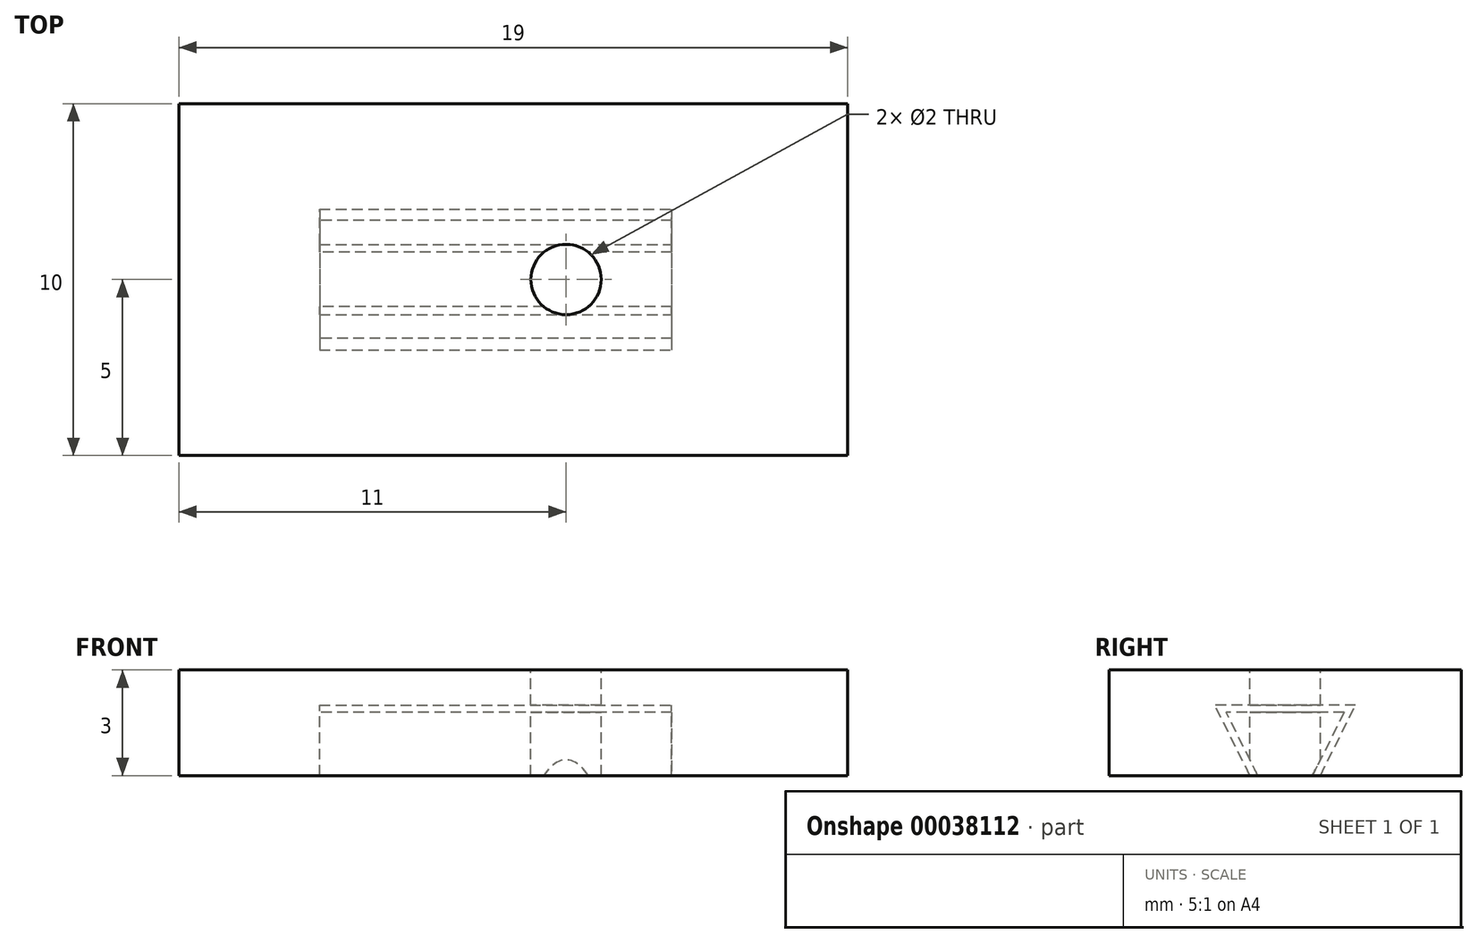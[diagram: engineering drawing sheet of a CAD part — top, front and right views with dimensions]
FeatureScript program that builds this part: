
annotation { "Feature Type Name" : "Feature", "Feature Type Description" : "" }
export const myFeature = defineFeature(function(context is Context, id is Id, definition is map)
    precondition{}
    {
        {
            var Q0;
            Q0=qCreatedBy(makeId("Top.planeOp"),FACE);
            var sketch = newSketch(context, id + "F0", { "sketchPlane" : qUnion([Q0])});
            skLineSegment(sketch, "E0.bottom", {"start": v(0, -5) * mm, "end": v(-14, -5) * mm});
            skLineSegment(sketch, "E0.top", {"start": v(0, 5) * mm, "end": v(-14, 5) * mm});
            skLineSegment(sketch, "E0.left", {"start": v(0, -5) * mm, "end": v(0, 5) * mm});
            skLineSegment(sketch, "E0.right", {"start": v(-14, -5) * mm, "end": v(-14, 5) * mm});
            skPoint(sketch, "E1", {"position": v(0, 0) * mm});
            skSolve(sketch);
        }
        {
            assignVariable(context, id + "F1", {"name" : "holed", "anyValue" : 2});
        }
        {
            var Q0;
            Q0 = qSketchRegion(id + "F0", true);
            extrude(context, id + "F2", {"entities" : qUnion([Q0]), "depth" : 3 * mm});
        }
        {
            var Q0;
            Q0=makeQuery(id+"F2.opExtrude","SWEPT_FACE",FACE,{"disambiguationData":[OSD([sQuery(id+"F0.wireOp",EDGE,"E0.left")])]});
            var sketch = newSketch(context, id + "F3", { "sketchPlane" : qUnion([Q0])});
            skLineSegment(sketch, "E2", {"start": v(0, 0) * mm, "end": v(-1, 0) * mm});
            skLineSegment(sketch, "E3", {"start": v(-1, 0) * mm, "end": v(-2, 2) * mm});
            skLineSegment(sketch, "E4", {"start": v(-2, 2) * mm, "end": v(0, 2) * mm});
            skLineSegment(sketch, "E5.MirrorCS", {"start": v(2, 2) * mm, "end": v(0, 2) * mm});
            skLineSegment(sketch, "E6.MirrorCS", {"start": v(1, 0) * mm, "end": v(2, 2) * mm});
            skLineSegment(sketch, "E7.MirrorCS", {"start": v(0, 0) * mm, "end": v(1, 0) * mm});
            skSolve(sketch);
        }
        {
            var Q0;
            Q0 = qSketchRegion(id + "F3", true);
            extrude(context, id + "F4", {"entities" : qUnion([Q0]), "operationType" : NewBodyOperationType.REMOVE, "oppositeDirection" : true, "depth" : 10 * mm});
        }
        {
            var Q0;
            Q0=makeQuery(id+"F4.boolean.opBoolean","COPY",FACE,{"derivedFrom":makeQuery(id+"F4.opExtrude","CAP_FACE",FACE,{"disambiguationData":[OSD([sQuery(id+"F3.wireOp",EDGE,"E2"),sQuery(id+"F3.wireOp",EDGE,"E3"),sQuery(id+"F3.wireOp",EDGE,"E4"),sQuery(id+"F3.wireOp",EDGE,"E5.MirrorCS"),sQuery(id+"F3.wireOp",EDGE,"E6.MirrorCS"),sQuery(id+"F3.wireOp",EDGE,"E7.MirrorCS")])],"isStart":false})});
            var sketch = newSketch(context, id + "F5", { "sketchPlane" : qUnion([Q0])});
            skLineSegment(sketch, "E8.0", {"start": v(-0.82, 0.09) * mm, "end": v(-1.68, 1.8) * mm});
            skLineSegment(sketch, "E8.1", {"start": v(1.68, 1.8) * mm, "end": v(-1.68, 1.8) * mm});
            skLineSegment(sketch, "E8.2", {"start": v(0.82, 0.09) * mm, "end": v(1.68, 1.8) * mm});
            skLineSegment(sketch, "E9", {"start": v(-0.82, 0.09) * mm, "end": v(-0.78, 0) * mm});
            skLineSegment(sketch, "E10", {"start": v(-0.78, 0) * mm, "end": v(0, 0) * mm});
            skLineSegment(sketch, "E11.MirrorCS", {"start": v(0.78, 0) * mm, "end": v(0, 0) * mm});
            skLineSegment(sketch, "E12.MirrorCS", {"start": v(0.82, 0.09) * mm, "end": v(0.78, 0) * mm});
            skSolve(sketch);
        }
        {
            var Q0;
            Q0=makeQuery(id+"F5.imprint","IMPRINT",FACE,{"disambiguationData":[TD([[makeQuery(id+"F5.imprint","IMPRINT",EDGE,{"derivedFrom":sQuery(id+"F5.wireOp",EDGE,"E8.0")}),-1.0]])]});
            extrude(context, id + "F6", {"entities" : qUnion([Q0]), "depth" : 10 * mm});
        }
        {
            var Q0;
            Q0=makeQuery(id+"F2.opExtrude","SWEPT_FACE",FACE,{"disambiguationData":[OSD([sQuery(id+"F0.wireOp",EDGE,"E0.left")])]});
            var sketch = newSketch(context, id + "F7", { "sketchPlane" : qUnion([Q0])});
            skLineSegment(sketch, "E13.bottom", {"start": v(-5, 3) * mm, "end": v(5, 3) * mm});
            skLineSegment(sketch, "E13.top", {"start": v(-5, 0) * mm, "end": v(5, 0) * mm});
            skLineSegment(sketch, "E13.left", {"start": v(-5, 3) * mm, "end": v(-5, 0) * mm});
            skLineSegment(sketch, "E13.right", {"start": v(5, 3) * mm, "end": v(5, 0) * mm});
            skSolve(sketch);
        }
        {
            var Q0;
            Q0 = qSketchRegion(id + "F7", true);
            extrude(context, id + "F8", {"entities" : qUnion([Q0]), "operationType" : NewBodyOperationType.ADD, "depth" : 5 * mm});
        }
        {
            var Q0;
            Q0=makeQuery(id+"F2.opExtrude","CAP_FACE",FACE,{"disambiguationData":[OSD([sQuery(id+"F0.wireOp",EDGE,"E0.bottom"),sQuery(id+"F0.wireOp",EDGE,"E0.top"),sQuery(id+"F0.wireOp",EDGE,"E0.left"),sQuery(id+"F0.wireOp",EDGE,"E0.right")])],"isStart":false});
            var sketch = newSketch(context, id + "F9", { "sketchPlane" : qUnion([Q0])});
            skPoint(sketch, "E14", {"position": v(-3, 0) * mm});
            skSolve(sketch);
        }
        {
            var Q0;
            Q0=sQuery(id+"F9.wireOp",VERTEX,"E14");
            var Q1;
            Q1=makeQuery(id+"F2.opExtrude","SWEPT_BODY",BODY,{"disambiguationData":[OSD([sQuery(id+"F0.wireOp",EDGE,"E0.bottom"),sQuery(id+"F0.wireOp",EDGE,"E0.top"),sQuery(id+"F0.wireOp",EDGE,"E0.left"),sQuery(id+"F0.wireOp",EDGE,"E0.right")])]});
            var Q2;
            Q2=makeQuery(id+"F6.opExtrude","SWEPT_BODY",BODY,{"disambiguationData":[OSD([sQuery(id+"F5.wireOp",EDGE,"E8.0"),sQuery(id+"F5.wireOp",EDGE,"E8.1"),sQuery(id+"F5.wireOp",EDGE,"E8.2"),sQuery(id+"F5.wireOp",EDGE,"E9"),sQuery(id+"F5.wireOp",EDGE,"E10"),sQuery(id+"F5.wireOp",EDGE,"E11.MirrorCS"),sQuery(id+"F5.wireOp",EDGE,"E12.MirrorCS")])]});
            hole(context, id + "F10", {"style" : HoleStyle.SIMPLE, "holeDiameter" : (getVariable(context, 'holed')) * mm, "endStyle" : HoleEndStyle.THROUGH, "locations" : qUnion([Q0]), "scope" : qUnion([Q1, Q2])});
        }
    });
